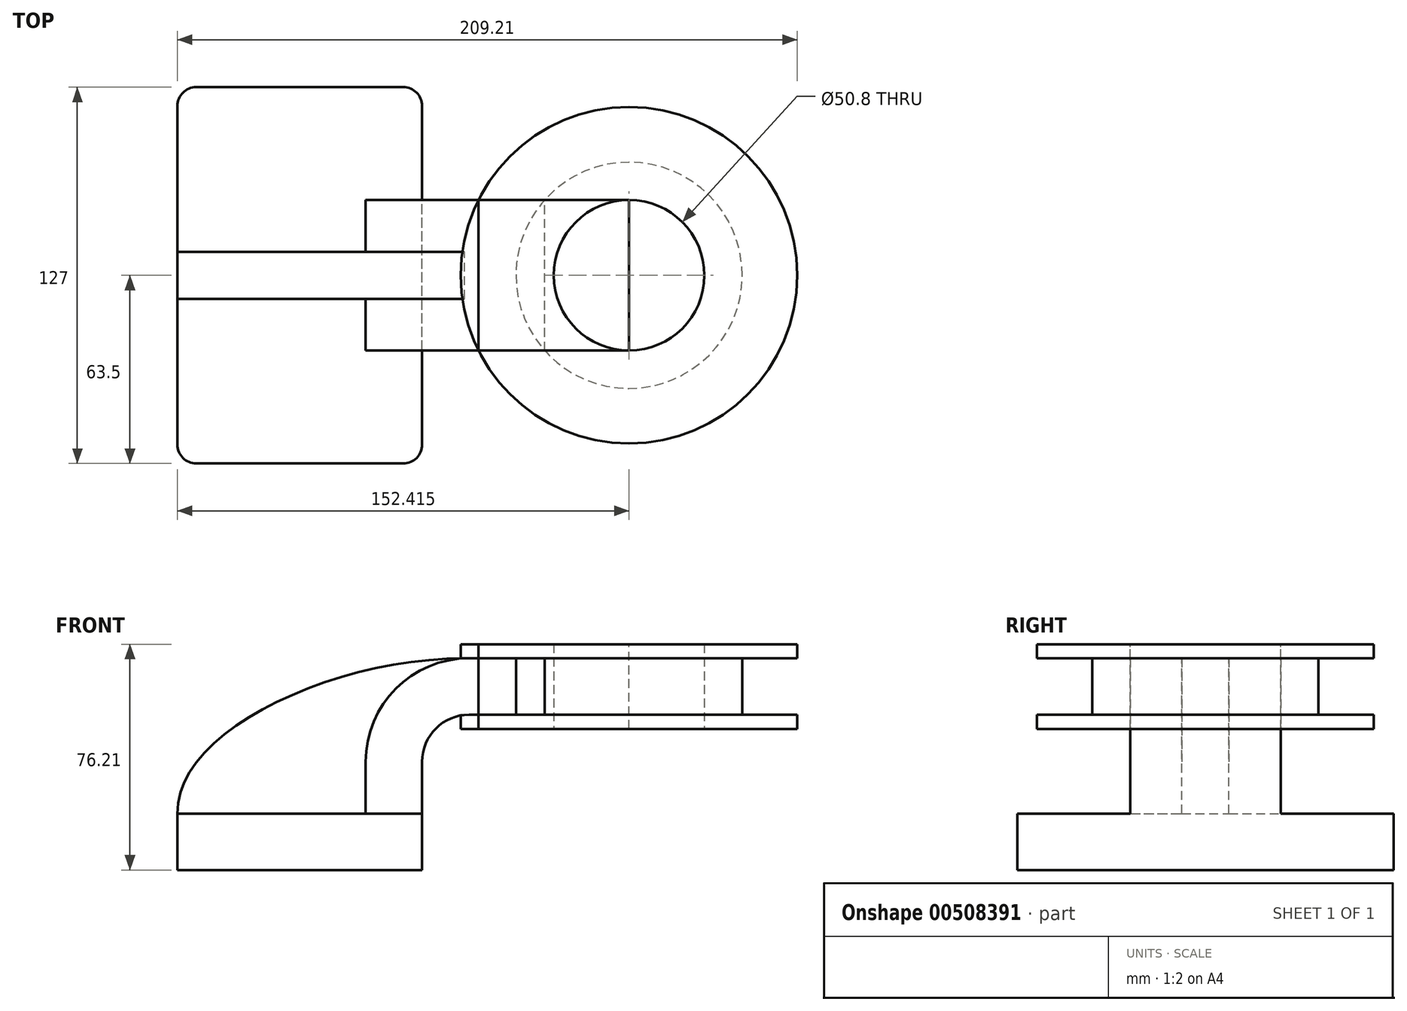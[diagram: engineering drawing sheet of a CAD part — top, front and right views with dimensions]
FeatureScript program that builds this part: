
annotation { "Feature Type Name" : "Feature", "Feature Type Description" : "" }
export const myFeature = defineFeature(function(context is Context, id is Id, definition is map)
    precondition{}
    {
        {
            var Q0;
            Q0=qCreatedBy(makeId("Front.planeOp"),FACE);
            var sketch = newSketch(context, id + "F0", { "sketchPlane" : qUnion([Q0])});
            skLineSegment(sketch, "E0.bottom", {"start": v(41.28, -9.52) * mm, "end": v(-41.28, -9.53) * mm});
            skLineSegment(sketch, "E0.top", {"start": v(41.28, 9.53) * mm, "end": v(-41.28, 9.53) * mm});
            skLineSegment(sketch, "E0.left", {"start": v(41.28, -9.52) * mm, "end": v(41.28, 9.53) * mm});
            skLineSegment(sketch, "E0.right", {"start": v(-41.28, -9.53) * mm, "end": v(-41.28, 9.53) * mm});
            skPoint(sketch, "E0.middle", {"position": v(0, 0) * mm});
            skLineSegment(sketch, "E1.bottom", {"start": v(111.12, 38.1) * mm, "end": v(60.32, 38.1) * mm});
            skLineSegment(sketch, "E1.top", {"start": v(111.12, 66.68) * mm, "end": v(60.32, 66.68) * mm});
            skLineSegment(sketch, "E1.left", {"start": v(111.12, 38.1) * mm, "end": v(111.12, 66.68) * mm});
            skLineSegment(sketch, "E1.right", {"start": v(60.32, 38.1) * mm, "end": v(60.32, 66.67) * mm});
            skPoint(sketch, "E1.middle", {"position": v(85.72, 52.39) * mm});
            skLineSegment(sketch, "E2", {"start": v(41.28, 9.53) * mm, "end": v(41.28, 27) * mm});
            skArc(sketch, "E3", {"start": v(41.27, 27) * mm, "mid": v(45.92, 38.23) * mm, "end": v(57.15, 42.88) * mm});
            skLineSegment(sketch, "E4", {"start": v(57.15, 42.88) * mm, "end": v(82.63, 42.88) * mm});
            skLineSegment(sketch, "E5.0", {"start": v(57.15, 61.93) * mm, "end": v(82.63, 61.93) * mm});
            skArc(sketch, "E5.1", {"start": v(22.23, 27) * mm, "mid": v(32.45, 51.7) * mm, "end": v(57.15, 61.93) * mm});
            skLineSegment(sketch, "E5.2", {"start": v(22.23, 9.53) * mm, "end": v(22.23, 27) * mm});
            skLineSegment(sketch, "E6", {"start": v(82.63, 42.88) * mm, "end": v(82.63, 61.93) * mm});
            skFitSpline(sketch, "E7", {"points": [v(-41.28, 9.53) * mm, v(55.57, 61.89) * mm], "startDerivative": vector(-2.72, 81.8) * mm, "endDerivative": vector(136.04, 0.04) * mm});
            skSolve(sketch);
        }
        {
            var Q0;
            Q0=makeQuery(id+"F0.imprint","IMPRINT",FACE,{"disambiguationData":[TD([[makeQuery(id+"F0.imprint","IMPRINT",EDGE,{"derivedFrom":sQuery(id+"F0.wireOp",EDGE,"E0.bottom")}),-1.0]])]});
            extrude(context, id + "F1", {"entities" : qUnion([Q0]), "endBound" : BoundingType.SYMMETRIC, "depth" : 127 * mm});
        }
        {
            var Q0;
            {var subQ1=sQuery(id+"F0.wireOp",EDGE,"E2");Q0=makeQuery(id+"F0.imprint","IMPRINT",FACE,{"disambiguationData":[TD([[makeQuery(id+"F0.imprint","IMPRINT",EDGE,{"derivedFrom":subQ1}),1.0]])]});}
            var Q1;
            {var subQ1=sQuery(id+"F0.wireOp",EDGE,"E1.bottom");Q1=makeQuery(id+"F0.imprint","IMPRINT",FACE,{"disambiguationData":[TD([[makeQuery(id+"F0.imprint","IMPRINT",EDGE,{"derivedFrom":subQ1}),-1.0]])]});}
            extrude(context, id + "F2", {"entities" : qUnion([Q0, Q1]), "operationType" : NewBodyOperationType.ADD, "endBound" : BoundingType.SYMMETRIC, "depth" : 50.8 * mm});
        }
        {
            var Q0;
            {var subQ2=sQuery(id+"F0.wireOp",EDGE,"E5.2");Q0=makeQuery(id+"F0.imprint","IMPRINT",FACE,{"disambiguationData":[TD([[makeQuery(id+"F0.imprint","IMPRINT",EDGE,{"derivedFrom":subQ2}),1.0]])]});}
            extrude(context, id + "F3", {"entities" : qUnion([Q0]), "operationType" : NewBodyOperationType.ADD, "endBound" : BoundingType.SYMMETRIC, "depth" : 15.88 * mm});
        }
        {
            var Q0;
            Q0=makeQuery(id+"F2.opExtrude","CAP_FACE",FACE,{"disambiguationData":[OSD([sQuery(id+"F0.wireOp",EDGE,"E1.bottom"),sQuery(id+"F0.wireOp",EDGE,"E1.top"),sQuery(id+"F0.wireOp",EDGE,"E1.left"),sQuery(id+"F0.wireOp",EDGE,"E1.right"),sQuery(id+"F0.wireOp",EDGE,"E4"),sQuery(id+"F0.wireOp",EDGE,"E5.0"),sQuery(id+"F0.wireOp",EDGE,"E6")])],"isStart":true});
            var Q1;
            Q1=sQuery(id+"F0.wireOp",EDGE,"E1.left");
            revolve(context, id + "F4", {"entities" : qUnion([Q0]), "axis" : qUnion([Q1]), "revolveType" : RevolveType.FULL});
        }
        {
            var Q0;
            Q0=makeQuery(id+"F1.opExtrude","CAP_EDGE",EDGE,{"disambiguationData":[OSD([sQuery(id+"F0.wireOp",EDGE,"E0.right")])],"isStart":false});
            var Q1;
            Q1=makeQuery(id+"F1.opExtrude","CAP_EDGE",EDGE,{"disambiguationData":[OSD([sQuery(id+"F0.wireOp",EDGE,"E0.left")])],"isStart":false});
            var Q2;
            Q2=makeQuery(id+"F1.opExtrude","CAP_EDGE",EDGE,{"disambiguationData":[OSD([sQuery(id+"F0.wireOp",EDGE,"E0.left")])],"isStart":true});
            var Q3;
            Q3=makeQuery(id+"F1.opExtrude","CAP_EDGE",EDGE,{"disambiguationData":[OSD([sQuery(id+"F0.wireOp",EDGE,"E0.right")])],"isStart":true});
            fillet(context, id + "F5", {"entities" : qUnion([Q0, Q1, Q2, Q3]), "radius" : 6.35 * mm, "tangentPropagation" : true, "allowEdgeOverflow" : false});
        }
    });
